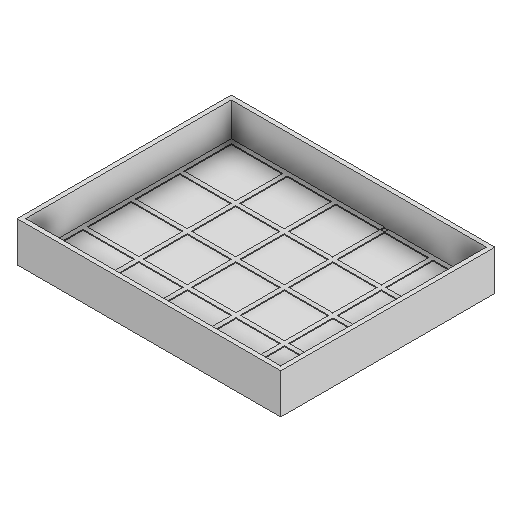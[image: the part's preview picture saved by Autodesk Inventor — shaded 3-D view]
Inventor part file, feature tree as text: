
AUTODESK INVENTOR PART (.ipt)
format: ipt  version: 2025.1 (Build 291241000, 241)  size: 243,712 bytes
history: native  units: mm
features: sketch x4, extrude x3
ambient origin geometry x8: Origin, YZ Plane, XZ Plane, XY Plane, X Axis, Y Axis, Z Axis, Center Point
bodies: Solid1 (feature_tree)
feature tree (7):
  extrude  "Extrusion1"  Depth=61.3mm
  extrude  "Extrusion2"  Depth=59.3mm
  extrude  "Extrusion3"  Depth=1.0mm
  sketch  "Sketch1"  dims[d0=49.8mm d1=61.3mm]
  sketch  "Sketch2"  dims[d5=47.8mm d6=1.0mm]
  sketch  "Sketch3"  dims[d7=1.0mm d8=8.0mm d9=0.0mm d10=1.0mm d12=1.0mm d13=12.0mm d14=1.0mm d15=12.0mm d16=1.0mm d17=1.0mm d18=10.25mm d19=10.25mm d20=2.0mm d21=1.0mm d22=1.0mm d23=50.0mm d25=11.3mm d26=10.0mm d28=10.0mm d30=0.2mm d31=0.0mm]
  sketch  "Sketch Rectangular Pattern1"  dims[d2=9.3mm d3=0.0mm d4=59.3mm]
